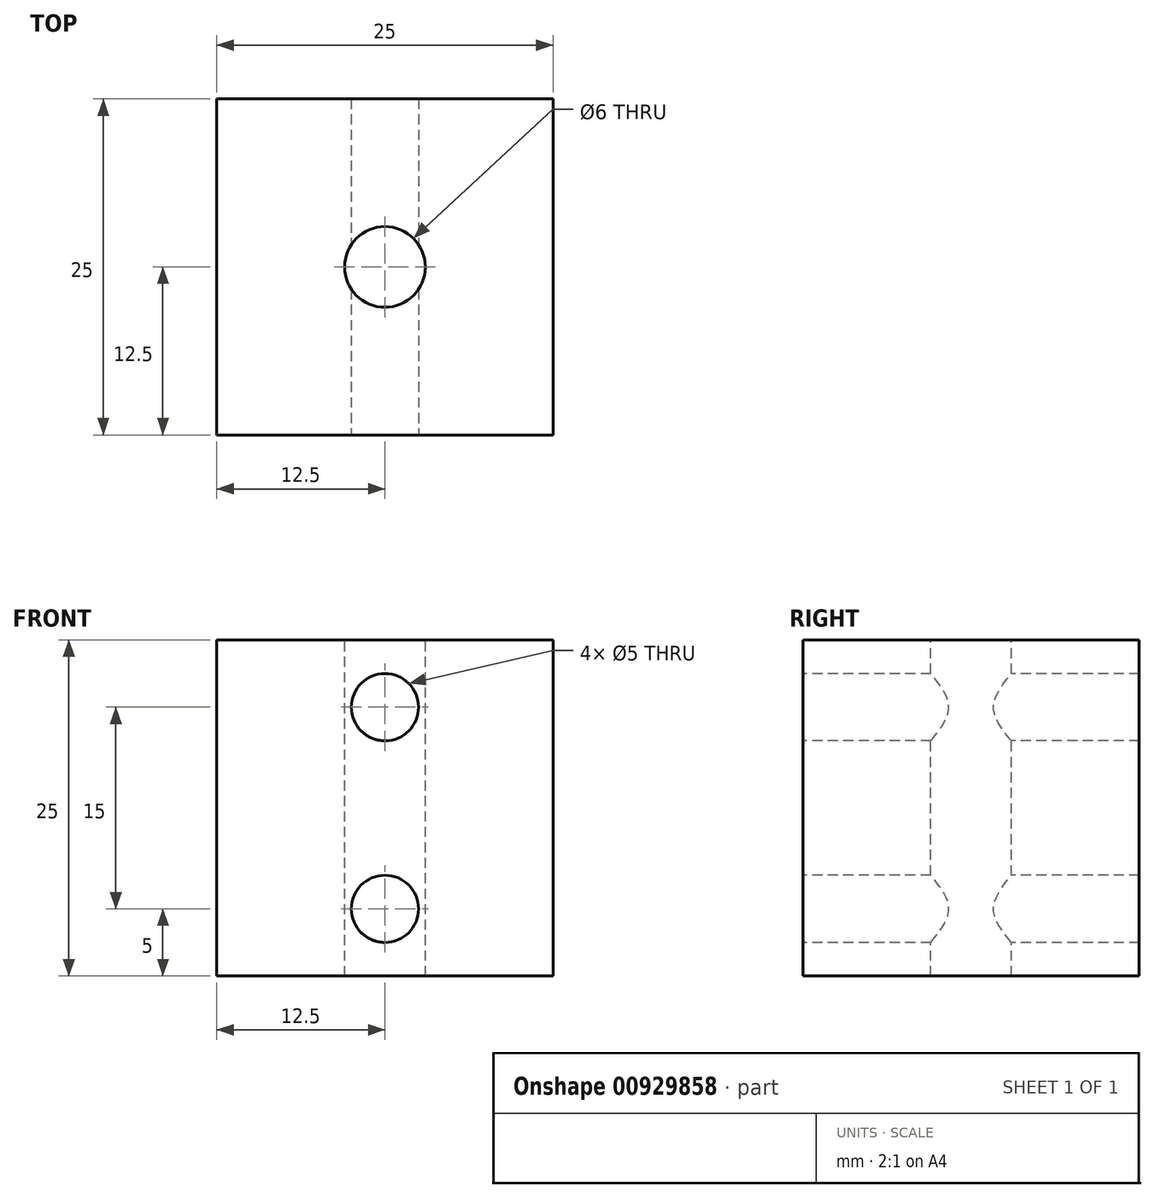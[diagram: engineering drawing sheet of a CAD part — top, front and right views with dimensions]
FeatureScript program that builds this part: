
annotation { "Feature Type Name" : "Feature", "Feature Type Description" : "" }
export const myFeature = defineFeature(function(context is Context, id is Id, definition is map)
    precondition{}
    {
        {
            var Q0;
            Q0=qCreatedBy(makeId("Top.planeOp"),FACE);
            var sketch = newSketch(context, id + "F0", { "sketchPlane" : qUnion([Q0])});
            skLineSegment(sketch, "E0.bottom", {"start": v(0, 0) * mm, "end": v(-25, 0) * mm});
            skLineSegment(sketch, "E0.top", {"start": v(0, 25) * mm, "end": v(-25, 25) * mm});
            skLineSegment(sketch, "E0.left", {"start": v(0, 0) * mm, "end": v(0, 25) * mm});
            skLineSegment(sketch, "E0.right", {"start": v(-25, 0) * mm, "end": v(-25, 25) * mm});
            skSolve(sketch);
        }
        {
            var Q0;
            Q0=makeQuery(id+"F0.imprint","IMPRINT",FACE,{"disambiguationData":[TD([[makeQuery(id+"F0.imprint","IMPRINT",EDGE,{"derivedFrom":sQuery(id+"F0.wireOp",EDGE,"E0.bottom")}),-1.0]])]});
            extrude(context, id + "F1", {"entities" : qUnion([Q0]), "depth" : 25 * mm, "offsetDistance" : 25 * mm});
        }
        {
            var Q0;
            Q0=makeQuery(id+"F1.opExtrude","CAP_FACE",FACE,{"disambiguationData":[OSD([sQuery(id+"F0.wireOp",EDGE,"E0.bottom"),sQuery(id+"F0.wireOp",EDGE,"E0.top"),sQuery(id+"F0.wireOp",EDGE,"E0.left"),sQuery(id+"F0.wireOp",EDGE,"E0.right")])],"isStart":false});
            var sketch = newSketch(context, id + "F2", { "sketchPlane" : qUnion([Q0])});
            skLineSegment(sketch, "E1", {"start": v(-12.5, 0) * mm, "end": v(-12.5, 25) * mm});
            skLineSegment(sketch, "E2", {"start": v(-12.5, 25) * mm, "end": v(-12.5, 12.5) * mm});
            skLineSegment(sketch, "E3", {"start": v(-12.5, 12.5) * mm, "end": v(0, 12.5) * mm});
            skSolve(sketch);
        }
        {
            var Q0;
            Q0=sQuery(id+"F2.wireOp",VERTEX,"E2.end");
            var Q1;
            Q1=makeQuery(id+"F1.opExtrude","SWEPT_BODY",BODY,{"disambiguationData":[OSD([sQuery(id+"F0.wireOp",EDGE,"E0.bottom"),sQuery(id+"F0.wireOp",EDGE,"E0.top"),sQuery(id+"F0.wireOp",EDGE,"E0.left"),sQuery(id+"F0.wireOp",EDGE,"E0.right")])]});
            hole(context, id + "F3", {"style" : HoleStyle.SIMPLE, "endStyle" : HoleEndStyle.THROUGH, "holeDiameter" : 6 * mm, "majorDiameter" : 5 * mm, "isTappedThrough" : true, "tappedDepth" : 12 * mm, "tapClearance" : 3, "locations" : qUnion([Q0]), "scope" : qUnion([Q1])});
        }
        {
            var Q0;
            Q0=makeQuery(id+"F1.opExtrude","SWEPT_FACE",FACE,{"disambiguationData":[OSD([sQuery(id+"F0.wireOp",EDGE,"E0.bottom")])]});
            var sketch = newSketch(context, id + "F4", { "sketchPlane" : qUnion([Q0])});
            skLineSegment(sketch, "E4", {"start": v(-12.5, 25) * mm, "end": v(-12.5, 20) * mm});
            skSolve(sketch);
        }
        {
            var Q0;
            Q0=sQuery(id+"F4.wireOp",VERTEX,"E4.end");
            var Q1;
            Q1=makeQuery(id+"F1.opExtrude","SWEPT_BODY",BODY,{"disambiguationData":[OSD([sQuery(id+"F0.wireOp",EDGE,"E0.bottom"),sQuery(id+"F0.wireOp",EDGE,"E0.top"),sQuery(id+"F0.wireOp",EDGE,"E0.left"),sQuery(id+"F0.wireOp",EDGE,"E0.right")])]});
            hole(context, id + "F5", {"style" : HoleStyle.SIMPLE, "endStyle" : HoleEndStyle.THROUGH, "standardTappedOrClearance" : lookupTablePath({ "standard" : "ISO", "engagement" : "75%", "pitch" : "1 mm", "size" : "M6", "type" : "Tapped" }), "standardBlindInLast" : lookupTablePath({ "standard" : "ISO", "fit" : "Normal", "engagement" : "75%", "pitch" : "1 mm", "size" : "M6", "type" : "Clearance & tapped" }), "holeDiameter" : 5 * mm, "majorDiameter" : 6 * mm, "showTappedDepth" : true, "isTappedThrough" : true, "tappedDepth" : 12 * mm, "tapClearance" : 3, "locations" : qUnion([Q0]), "scope" : qUnion([Q1])});
        }
        {
            var Q0;
            Q0=makeQuery(id+"F1.opExtrude","SWEPT_FACE",FACE,{"disambiguationData":[OSD([sQuery(id+"F0.wireOp",EDGE,"E0.bottom")])]});
            var sketch = newSketch(context, id + "F6", { "sketchPlane" : qUnion([Q0])});
            skLineSegment(sketch, "E5", {"start": v(-12.5, 0) * mm, "end": v(-12.5, 5) * mm});
            skSolve(sketch);
        }
        {
            var Q0;
            Q0=sQuery(id+"F6.wireOp",VERTEX,"E5.end");
            var Q1;
            Q1=makeQuery(id+"F1.opExtrude","SWEPT_BODY",BODY,{"disambiguationData":[OSD([sQuery(id+"F0.wireOp",EDGE,"E0.bottom"),sQuery(id+"F0.wireOp",EDGE,"E0.top"),sQuery(id+"F0.wireOp",EDGE,"E0.left"),sQuery(id+"F0.wireOp",EDGE,"E0.right")])]});
            hole(context, id + "F7", {"style" : HoleStyle.SIMPLE, "endStyle" : HoleEndStyle.THROUGH, "standardTappedOrClearance" : lookupTablePath({ "standard" : "ISO", "engagement" : "75%", "pitch" : "1 mm", "size" : "M6", "type" : "Tapped" }), "standardBlindInLast" : lookupTablePath({ "standard" : "ISO", "fit" : "Normal", "engagement" : "75%", "pitch" : "1 mm", "size" : "M6", "type" : "Clearance & tapped" }), "holeDiameter" : 5 * mm, "majorDiameter" : 6 * mm, "showTappedDepth" : true, "isTappedThrough" : true, "tappedDepth" : 12 * mm, "tapClearance" : 3, "locations" : qUnion([Q0]), "scope" : qUnion([Q1])});
        }
    });
